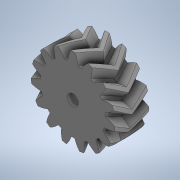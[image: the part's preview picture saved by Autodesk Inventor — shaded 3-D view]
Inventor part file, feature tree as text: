
AUTODESK INVENTOR PART (.ipt)
format: ipt  version: 2020 (Build 240168000, 168)  size: 530,432 bytes
history: native  units: mm (DEFAULTED — no unit token found)
features: plane x3, other x3, sketch x3, extrude x2, mirror x1
ambient origin geometry x8: Origin, YZ Plane, XZ Plane, XY Plane, X Axis, Y Axis, Z Axis, Center Point
bodies: Solid1 (feature_tree)
feature tree (12):
  extrude  "Extrusion1"  Depth=5.0mm TaperAngle=0.0deg
  plane  "Work Plane2"
  plane  "Work Plane8"
  plane  "Work Plane9"
  other  "Spur Gear"
  mirror  "Mirror1"
  extrude  "Extrusion2"  Depth=10.0mm TaperAngle=0.0deg
  sketch  "Sketch1"  dims[d0=24.663139mm d1=5.0mm d2=0.0mm]
  sketch  "Sketch2"  dims[d3=22.2mm d4=10.0mm d5=0.0mm]
  other  "Srf1"
  sketch  "Sketch3"  dims[d16=22.2mm d17=0.0mm d34=2.094395mm d39=0.0mm d41=0.0mm d43=22.2mm d46=22.2mm d47=0.0mm d48=0.0mm d49=3.2mm d50=10.0mm d51=0.0mm]
  other  "Pitch Diameter"
